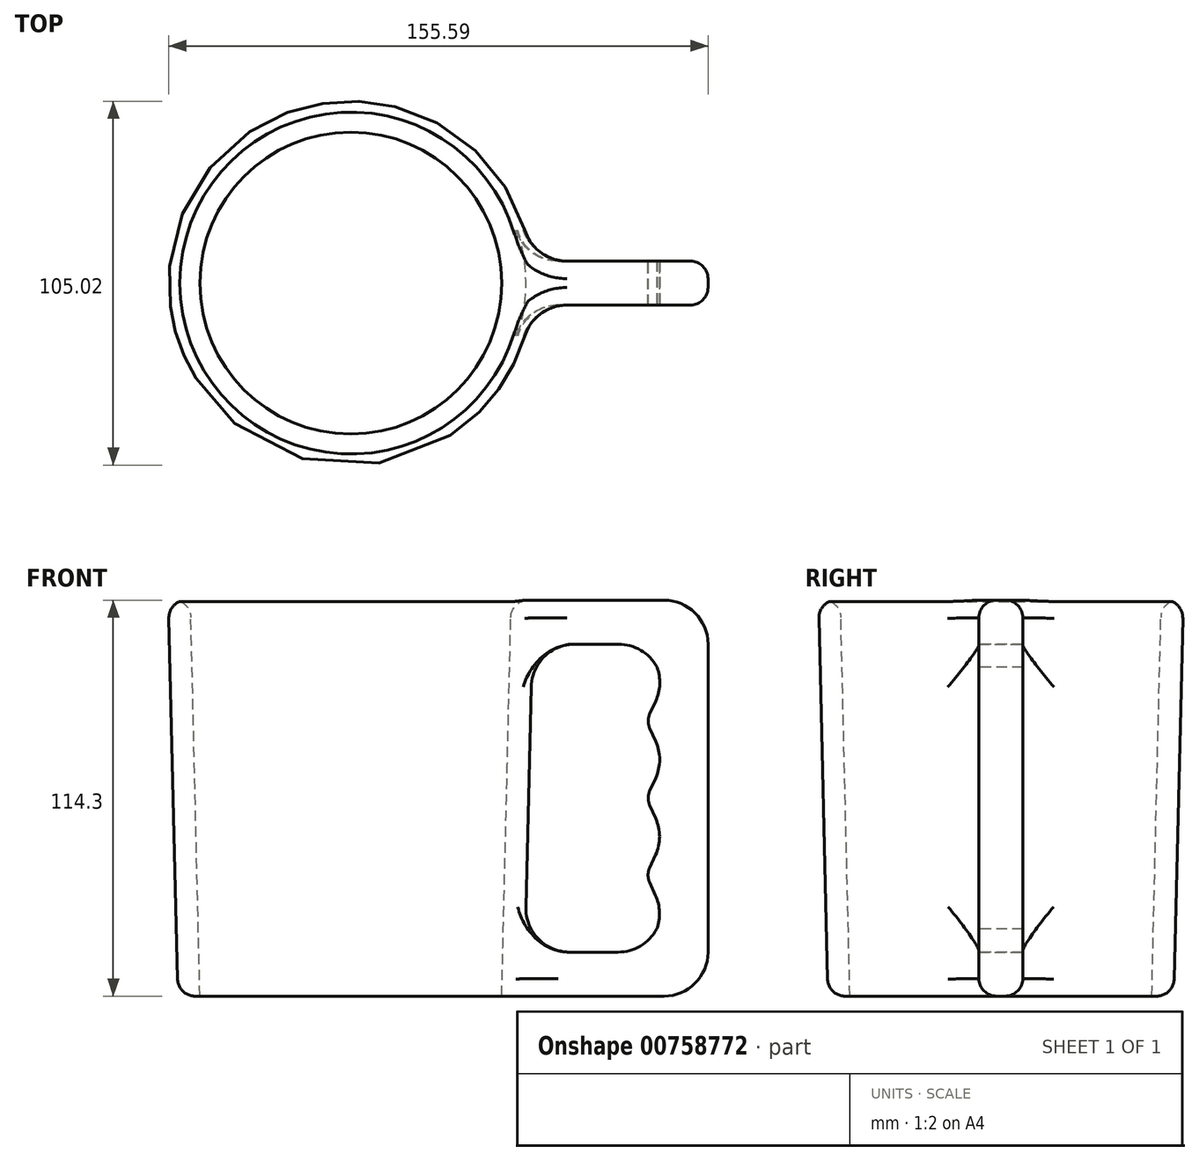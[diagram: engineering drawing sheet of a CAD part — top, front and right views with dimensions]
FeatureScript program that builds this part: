
annotation { "Feature Type Name" : "Feature", "Feature Type Description" : "" }
export const myFeature = defineFeature(function(context is Context, id is Id, definition is map)
    precondition{}
    {
        {
            var Q0;
            Q0=qCreatedBy(makeId("Front.planeOp"),FACE);
            var sketch = newSketch(context, id + "F0", { "sketchPlane" : qUnion([Q0])});
            skLineSegment(sketch, "E0", {"start": v(0, 0) * mm, "end": v(0, 127) * mm});
            skLineSegment(sketch, "E1", {"start": v(0, 0) * mm, "end": v(0, -127) * mm});
            skLineSegment(sketch, "E2", {"start": v(0, -127) * mm, "end": v(41.44, -127) * mm});
            skLineSegment(sketch, "E3", {"start": v(0, 127) * mm, "end": v(47.5, 127) * mm});
            skLineSegment(sketch, "E4", {"start": v(47.5, 127) * mm, "end": v(41.44, -127) * mm});
            skLineSegment(sketch, "E5", {"start": v(0, 63.5) * mm, "end": v(45.98, 63.5) * mm});
            skLineSegment(sketch, "E6", {"start": v(47.5, 127) * mm, "end": v(53.85, 127) * mm});
            skLineSegment(sketch, "E7", {"start": v(53.85, 127) * mm, "end": v(47.79, -127) * mm});
            skLineSegment(sketch, "E8", {"start": v(47.79, -127) * mm, "end": v(41.44, -127) * mm});
            skLineSegment(sketch, "E9", {"start": v(0, 63.5) * mm, "end": v(0, 127) * mm});
            skLineSegment(sketch, "E10", {"start": v(103.13, 76.2) * mm, "end": v(52.64, 76.2) * mm});
            skLineSegment(sketch, "E11", {"start": v(103.08, -25.4) * mm, "end": v(103.08, -38.1) * mm});
            skLineSegment(sketch, "E12", {"start": v(103.08, -38.1) * mm, "end": v(49.9, -38.1) * mm});
            skLineSegment(sketch, "E13", {"start": v(103.08, 76.2) * mm, "end": v(103.13, 76.2) * mm});
            skLineSegment(sketch, "E14", {"start": v(103.08, 76.2) * mm, "end": v(103.08, -25.4) * mm});
            skLineSegment(sketch, "E15", {"start": v(100.6, -25.4) * mm, "end": v(50.21, -25.4) * mm});
            skLineSegment(sketch, "E16", {"start": v(52.64, 76.2) * mm, "end": v(46.29, 76.2) * mm});
            skLineSegment(sketch, "E17", {"start": v(46.29, 76.2) * mm, "end": v(45.98, 63.5) * mm});
            skLineSegment(sketch, "E18", {"start": v(52.33, 63.5) * mm, "end": v(45.98, 63.5) * mm});
            skLineSegment(sketch, "E19", {"start": v(50.21, -25.4) * mm, "end": v(43.86, -25.4) * mm});
            skLineSegment(sketch, "E20", {"start": v(43.86, -25.4) * mm, "end": v(43.56, -38.1) * mm});
            skLineSegment(sketch, "E21", {"start": v(43.56, -38.1) * mm, "end": v(49.9, -38.1) * mm});
            skLineSegment(sketch, "E22", {"start": v(90.38, 30.17) * mm, "end": v(85.31, 19.05) * mm});
            skLineSegment(sketch, "E23", {"start": v(85.31, 19.05) * mm, "end": v(90.37, 7.93) * mm});
            skLineSegment(sketch, "E24", {"start": v(90.37, 7.93) * mm, "end": v(85.27, -3.17) * mm});
            skLineSegment(sketch, "E25", {"start": v(85.27, -3.17) * mm, "end": v(90.35, -14.29) * mm});
            skLineSegment(sketch, "E26", {"start": v(90.35, -14.29) * mm, "end": v(85.27, -25.4) * mm});
            skLineSegment(sketch, "E27", {"start": v(85.27, -25.4) * mm, "end": v(43.86, -25.4) * mm});
            skLineSegment(sketch, "E28", {"start": v(90.38, 30.17) * mm, "end": v(85.31, 41.29) * mm});
            skLineSegment(sketch, "E29", {"start": v(85.31, 41.29) * mm, "end": v(90.43, 52.38) * mm});
            skLineSegment(sketch, "E30", {"start": v(90.43, 52.38) * mm, "end": v(85.36, 63.5) * mm});
            skLineSegment(sketch, "E31", {"start": v(85.36, 63.5) * mm, "end": v(45.98, 63.5) * mm});
            skLineSegment(sketch, "E32", {"start": v(90.38, 30.17) * mm, "end": v(103.08, 30.17) * mm});
            skSolve(sketch);
        }
        {
            var Q0;
            Q0=makeQuery(id+"F0.imprint","IMPRINT",FACE,{"disambiguationData":[TD([[makeQuery(id+"F0.imprint","IMPRINT",EDGE,{"derivedFrom":sQuery(id+"F0.wireOp",EDGE,"E28")}),-1.0]])]});
            var Q1;
            {var subQ2=sQuery(id+"F0.wireOp",EDGE,"E16");Q1=makeQuery(id+"F0.imprint","IMPRINT",FACE,{"disambiguationData":[TD([[makeQuery(id+"F0.imprint","IMPRINT",EDGE,{"derivedFrom":subQ2}),1.0]])]});}
            var Q2;
            {var subQ2=sQuery(id+"F0.wireOp",EDGE,"E19");Q2=makeQuery(id+"F0.imprint","IMPRINT",FACE,{"disambiguationData":[TD([[makeQuery(id+"F0.imprint","IMPRINT",EDGE,{"derivedFrom":subQ2}),1.0]])]});}
            var Q3;
            {var subQ6=sQuery(id+"F0.wireOp",EDGE,"E11");Q3=makeQuery(id+"F0.imprint","IMPRINT",FACE,{"disambiguationData":[TD([[makeQuery(id+"F0.imprint","IMPRINT",EDGE,{"derivedFrom":subQ6}),-1.0]])]});}
            extrude(context, id + "F1", {"entities" : qUnion([Q0, Q1, Q2, Q3]), "endBound" : BoundingType.SYMMETRIC, "depth" : 12.7 * mm, "offsetDistance" : 25.4 * mm});
        }
        {
            var Q0;
            {var subQ0=sQuery(id+"F0.wireOp",EDGE,"E18");Q0=makeQuery(id+"F0.imprint","IMPRINT",FACE,{"disambiguationData":[TD([[makeQuery(id+"F0.imprint","IMPRINT",EDGE,{"derivedFrom":subQ0}),1.0]])]});}
            var Q1;
            {var subQ2=sQuery(id+"F0.wireOp",EDGE,"E16");Q1=makeQuery(id+"F0.imprint","IMPRINT",FACE,{"disambiguationData":[TD([[makeQuery(id+"F0.imprint","IMPRINT",EDGE,{"derivedFrom":subQ2}),1.0]])]});}
            var Q2;
            {var subQ2=sQuery(id+"F0.wireOp",EDGE,"E19");Q2=makeQuery(id+"F0.imprint","IMPRINT",FACE,{"disambiguationData":[TD([[makeQuery(id+"F0.imprint","IMPRINT",EDGE,{"derivedFrom":subQ2}),1.0]])]});}
            var Q3;
            {var subQ0=sQuery(id+"F0.wireOp",EDGE,"E18");Q3=makeQuery(id+"F0.imprint","IMPRINT",FACE,{"disambiguationData":[TD([[makeQuery(id+"F0.imprint","IMPRINT",EDGE,{"derivedFrom":subQ0}),1.0]])]});}
            var Q4;
            {var subQ2=sQuery(id+"F0.wireOp",EDGE,"E19");Q4=makeQuery(id+"F0.imprint","IMPRINT",FACE,{"disambiguationData":[TD([[makeQuery(id+"F0.imprint","IMPRINT",EDGE,{"derivedFrom":subQ2}),1.0]])]});}
            var Q5;
            Q5=sQuery(id+"F0.wireOp",EDGE,"E0");
            revolve(context, id + "F2", {"operationType" : NewBodyOperationType.ADD, "surfaceOperationType" : NewSurfaceOperationType.NEW, "entities" : qUnion([Q0, Q1, Q2, Q3, Q4]), "axis" : qUnion([Q5]), "revolveType" : RevolveType.FULL});
        }
        {
            var Q0;
            Q0=makeQuery(id+"F1.opExtrude","SWEPT_EDGE",EDGE,{"disambiguationData":[OSD([sQuery(id+"F0.wireOp",EDGE,"E30"),sQuery(id+"F0.wireOp",EDGE,"E31")])]});
            var Q1;
            Q1=makeQuery(id+"F1.opExtrude","SWEPT_EDGE",EDGE,{"disambiguationData":[OSD([sQuery(id+"F0.wireOp",EDGE,"E29"),sQuery(id+"F0.wireOp",EDGE,"E30")])]});
            var Q2;
            Q2=makeQuery(id+"F1.opExtrude","SWEPT_EDGE",EDGE,{"disambiguationData":[OSD([sQuery(id+"F0.wireOp",EDGE,"E22"),sQuery(id+"F0.wireOp",EDGE,"E28"),sQuery(id+"F0.wireOp",EDGE,"E32")])]});
            var Q3;
            Q3=makeQuery(id+"F1.opExtrude","SWEPT_EDGE",EDGE,{"disambiguationData":[OSD([sQuery(id+"F0.wireOp",EDGE,"E23"),sQuery(id+"F0.wireOp",EDGE,"E24")])]});
            var Q4;
            Q4=makeQuery(id+"F1.opExtrude","SWEPT_EDGE",EDGE,{"disambiguationData":[OSD([sQuery(id+"F0.wireOp",EDGE,"E25"),sQuery(id+"F0.wireOp",EDGE,"E26")])]});
            var Q5;
            Q5=makeQuery(id+"F1.opExtrude","SWEPT_EDGE",EDGE,{"disambiguationData":[OSD([sQuery(id+"F0.wireOp",EDGE,"E15"),sQuery(id+"F0.wireOp",EDGE,"E26")])]});
            var Q6;
            Q6=makeQuery(id+"F1.opExtrude","SWEPT_EDGE",EDGE,{"disambiguationData":[OSD([sQuery(id+"F0.wireOp",EDGE,"E11"),sQuery(id+"F0.wireOp",EDGE,"E12")])]});
            var Q7;
            Q7=makeQuery(id+"F1.opExtrude","SWEPT_EDGE",EDGE,{"disambiguationData":[OSD([sQuery(id+"F0.wireOp",EDGE,"E10"),sQuery(id+"F0.wireOp",EDGE,"E14")])]});
            var Q8;
            Q8=makeQuery(id+"F2.boolean.opBoolean","INTERSECT",EDGE,{"disambiguationData":[OD(1.0)],"derivedFrom":[makeQuery(id+"F1.opExtrude","CAP_FACE",FACE,{"disambiguationData":[OSD([sQuery(id+"F0.wireOp",EDGE,"E4"),sQuery(id+"F0.wireOp",EDGE,"E10"),sQuery(id+"F0.wireOp",EDGE,"E11"),sQuery(id+"F0.wireOp",EDGE,"E12"),sQuery(id+"F0.wireOp",EDGE,"E14"),sQuery(id+"F0.wireOp",EDGE,"E15"),sQuery(id+"F0.wireOp",EDGE,"E16"),sQuery(id+"F0.wireOp",EDGE,"E18"),sQuery(id+"F0.wireOp",EDGE,"E19"),sQuery(id+"F0.wireOp",EDGE,"E21"),sQuery(id+"F0.wireOp",EDGE,"E22"),sQuery(id+"F0.wireOp",EDGE,"E23"),sQuery(id+"F0.wireOp",EDGE,"E24"),sQuery(id+"F0.wireOp",EDGE,"E25"),sQuery(id+"F0.wireOp",EDGE,"E26"),sQuery(id+"F0.wireOp",EDGE,"E28"),sQuery(id+"F0.wireOp",EDGE,"E29"),sQuery(id+"F0.wireOp",EDGE,"E30"),sQuery(id+"F0.wireOp",EDGE,"E31")])],"isStart":false}),makeQuery(id+"F2.opRevolve","SWEPT_FACE",FACE,{"disambiguationData":[OSD([sQuery(id+"F0.wireOp",EDGE,"E7")])]})]});
            var Q9;
            Q9=makeQuery(id+"F2.boolean.opBoolean","INTERSECT",EDGE,{"disambiguationData":[OD(1.0)],"derivedFrom":[makeQuery(id+"F1.opExtrude","CAP_FACE",FACE,{"disambiguationData":[OSD([sQuery(id+"F0.wireOp",EDGE,"E4"),sQuery(id+"F0.wireOp",EDGE,"E10"),sQuery(id+"F0.wireOp",EDGE,"E11"),sQuery(id+"F0.wireOp",EDGE,"E12"),sQuery(id+"F0.wireOp",EDGE,"E14"),sQuery(id+"F0.wireOp",EDGE,"E15"),sQuery(id+"F0.wireOp",EDGE,"E16"),sQuery(id+"F0.wireOp",EDGE,"E18"),sQuery(id+"F0.wireOp",EDGE,"E19"),sQuery(id+"F0.wireOp",EDGE,"E21"),sQuery(id+"F0.wireOp",EDGE,"E22"),sQuery(id+"F0.wireOp",EDGE,"E23"),sQuery(id+"F0.wireOp",EDGE,"E24"),sQuery(id+"F0.wireOp",EDGE,"E25"),sQuery(id+"F0.wireOp",EDGE,"E26"),sQuery(id+"F0.wireOp",EDGE,"E28"),sQuery(id+"F0.wireOp",EDGE,"E29"),sQuery(id+"F0.wireOp",EDGE,"E30"),sQuery(id+"F0.wireOp",EDGE,"E31")])],"isStart":true}),makeQuery(id+"F2.opRevolve","SWEPT_FACE",FACE,{"disambiguationData":[OSD([sQuery(id+"F0.wireOp",EDGE,"E7")])]})]});
            var Q10;
            Q10=makeQuery(id+"F2.boolean.opBoolean","INTERSECT",EDGE,{"derivedFrom":[makeQuery(id+"F1.opExtrude","SWEPT_FACE",FACE,{"disambiguationData":[OSD([sQuery(id+"F0.wireOp",EDGE,"E15"),sQuery(id+"F0.wireOp",EDGE,"E19")])]}),makeQuery(id+"F2.opRevolve","SWEPT_FACE",FACE,{"disambiguationData":[OSD([sQuery(id+"F0.wireOp",EDGE,"E7")])]})]});
            var Q11;
            Q11=makeQuery(id+"F2.boolean.opBoolean","INTERSECT",EDGE,{"disambiguationData":[OD(0.0)],"derivedFrom":[makeQuery(id+"F1.opExtrude","CAP_FACE",FACE,{"disambiguationData":[OSD([sQuery(id+"F0.wireOp",EDGE,"E4"),sQuery(id+"F0.wireOp",EDGE,"E10"),sQuery(id+"F0.wireOp",EDGE,"E11"),sQuery(id+"F0.wireOp",EDGE,"E12"),sQuery(id+"F0.wireOp",EDGE,"E14"),sQuery(id+"F0.wireOp",EDGE,"E15"),sQuery(id+"F0.wireOp",EDGE,"E16"),sQuery(id+"F0.wireOp",EDGE,"E18"),sQuery(id+"F0.wireOp",EDGE,"E19"),sQuery(id+"F0.wireOp",EDGE,"E21"),sQuery(id+"F0.wireOp",EDGE,"E22"),sQuery(id+"F0.wireOp",EDGE,"E23"),sQuery(id+"F0.wireOp",EDGE,"E24"),sQuery(id+"F0.wireOp",EDGE,"E25"),sQuery(id+"F0.wireOp",EDGE,"E26"),sQuery(id+"F0.wireOp",EDGE,"E28"),sQuery(id+"F0.wireOp",EDGE,"E29"),sQuery(id+"F0.wireOp",EDGE,"E30"),sQuery(id+"F0.wireOp",EDGE,"E31")])],"isStart":false}),makeQuery(id+"F2.opRevolve","SWEPT_FACE",FACE,{"disambiguationData":[OSD([sQuery(id+"F0.wireOp",EDGE,"E7")])]})]});
            var Q12;
            Q12=makeQuery(id+"F2.boolean.opBoolean","INTERSECT",EDGE,{"disambiguationData":[OD(0.0)],"derivedFrom":[makeQuery(id+"F1.opExtrude","CAP_FACE",FACE,{"disambiguationData":[OSD([sQuery(id+"F0.wireOp",EDGE,"E4"),sQuery(id+"F0.wireOp",EDGE,"E10"),sQuery(id+"F0.wireOp",EDGE,"E11"),sQuery(id+"F0.wireOp",EDGE,"E12"),sQuery(id+"F0.wireOp",EDGE,"E14"),sQuery(id+"F0.wireOp",EDGE,"E15"),sQuery(id+"F0.wireOp",EDGE,"E16"),sQuery(id+"F0.wireOp",EDGE,"E18"),sQuery(id+"F0.wireOp",EDGE,"E19"),sQuery(id+"F0.wireOp",EDGE,"E21"),sQuery(id+"F0.wireOp",EDGE,"E22"),sQuery(id+"F0.wireOp",EDGE,"E23"),sQuery(id+"F0.wireOp",EDGE,"E24"),sQuery(id+"F0.wireOp",EDGE,"E25"),sQuery(id+"F0.wireOp",EDGE,"E26"),sQuery(id+"F0.wireOp",EDGE,"E28"),sQuery(id+"F0.wireOp",EDGE,"E29"),sQuery(id+"F0.wireOp",EDGE,"E30"),sQuery(id+"F0.wireOp",EDGE,"E31")])],"isStart":true}),makeQuery(id+"F2.opRevolve","SWEPT_FACE",FACE,{"disambiguationData":[OSD([sQuery(id+"F0.wireOp",EDGE,"E7")])]})]});
            var Q13;
            Q13=makeQuery(id+"F2.boolean.opBoolean","INTERSECT",EDGE,{"derivedFrom":[makeQuery(id+"F1.opExtrude","SWEPT_FACE",FACE,{"disambiguationData":[OSD([sQuery(id+"F0.wireOp",EDGE,"E18"),sQuery(id+"F0.wireOp",EDGE,"E31")])]}),makeQuery(id+"F2.opRevolve","SWEPT_FACE",FACE,{"disambiguationData":[OSD([sQuery(id+"F0.wireOp",EDGE,"E7")])]})]});
            fillet(context, id + "F3", {"entities" : qUnion([Q0, Q1, Q2, Q3, Q4, Q5, Q6, Q7, Q8, Q9, Q10, Q11, Q12, Q13]), "radius" : 12.7 * mm, "tangentPropagation" : true, "allowEdgeOverflow" : false});
        }
        {
            var Q0;
            {var subQ0=sQuery(id+"F0.wireOp",EDGE,"E16");Q0=makeQuery(id+"F2.boolean.opBoolean","MERGE",FACE,{"derivedFrom":[makeQuery(id+"F1.opExtrude","SWEPT_FACE",FACE,{"disambiguationData":[OSD([sQuery(id+"F0.wireOp",EDGE,"E10"),subQ0])]}),makeQuery(id+"F2.opRevolve","SWEPT_FACE",FACE,{"disambiguationData":[OSD([subQ0])]})]});}
            var Q1;
            Q1=makeQuery(id+"F1.opExtrude","SWEPT_EDGE",EDGE,{"disambiguationData":[OSD([sQuery(id+"F0.wireOp",EDGE,"E24"),sQuery(id+"F0.wireOp",EDGE,"E25")])]});
            var Q2;
            Q2=makeQuery(id+"F1.opExtrude","SWEPT_EDGE",EDGE,{"disambiguationData":[OSD([sQuery(id+"F0.wireOp",EDGE,"E22"),sQuery(id+"F0.wireOp",EDGE,"E23")])]});
            var Q3;
            Q3=makeQuery(id+"F1.opExtrude","SWEPT_EDGE",EDGE,{"disambiguationData":[OSD([sQuery(id+"F0.wireOp",EDGE,"E28"),sQuery(id+"F0.wireOp",EDGE,"E29")])]});
            fillet(context, id + "F4", {"entities" : qUnion([Q0, Q1, Q2, Q3]), "radius" : 5.08 * mm, "tangentPropagation" : true, "allowEdgeOverflow" : false});
        }
    });
